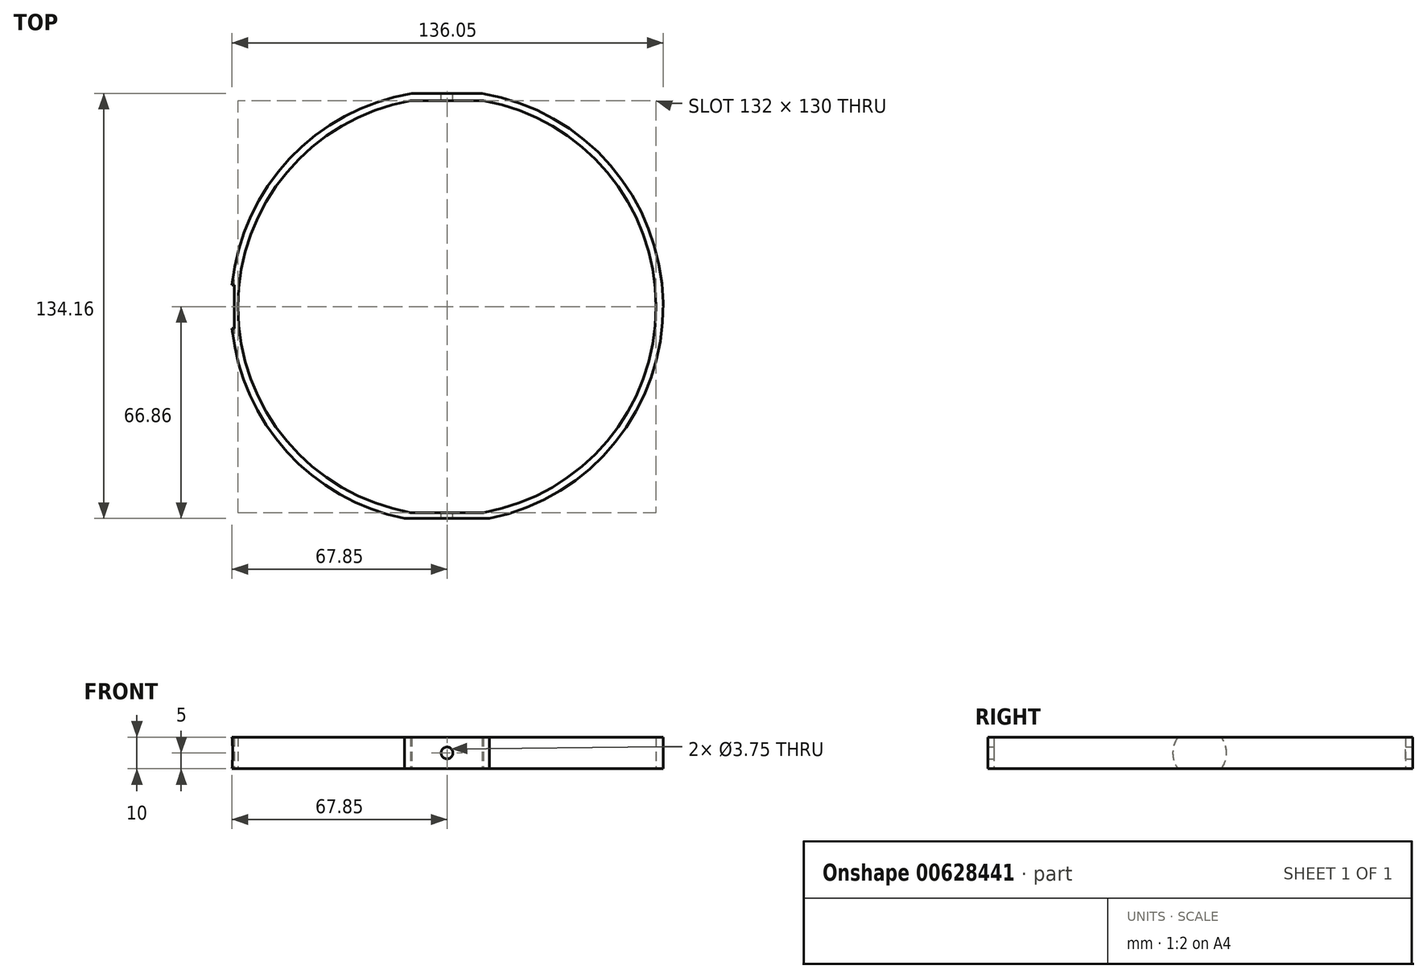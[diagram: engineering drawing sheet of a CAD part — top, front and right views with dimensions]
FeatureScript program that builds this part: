
annotation { "Feature Type Name" : "Feature", "Feature Type Description" : "" }
export const myFeature = defineFeature(function(context is Context, id is Id, definition is map)
    precondition{}
    {
        {
            var Q0;
            Q0=qCreatedBy(makeId("Top.planeOp"),FACE);
            var sketch = newSketch(context, id + "F0", { "sketchPlane" : qUnion([Q0])});
            skLineSegment(sketch, "E0", {"start": v(0, 0) * mm, "end": v(0, 65) * mm});
            skLineSegment(sketch, "E1", {"start": v(0, 0) * mm, "end": v(-66, 0) * mm});
            skArc(sketch, "E2", {"start": v(-11.45, 65) * mm, "mid": v(-66, 0) * mm, "end": v(-11.45, -65) * mm});
            skLineSegment(sketch, "E3.MirrorCS", {"start": v(0, 0) * mm, "end": v(66, 0) * mm});
            skLineSegment(sketch, "E4.MirrorCS", {"start": v(0, 0) * mm, "end": v(0, -65) * mm});
            skLineSegment(sketch, "E5", {"start": v(0, 65) * mm, "end": v(-11.45, 65) * mm});
            skLineSegment(sketch, "E6", {"start": v(-11.45, 65) * mm, "end": v(11.45, 65) * mm});
            skLineSegment(sketch, "E7", {"start": v(0, -65) * mm, "end": v(-11.45, -65) * mm});
            skLineSegment(sketch, "E8", {"start": v(-11.45, -65) * mm, "end": v(11.45, -65) * mm});
            skArc(sketch, "E9.trimOffspring", {"start": v(11.45, -65) * mm, "mid": v(66, 0) * mm, "end": v(11.45, 65) * mm});
            skArc(sketch, "E10", {"start": v(13.44, -66.86) * mm, "mid": v(68.2, 1.2) * mm, "end": v(11.08, 67.3) * mm});
            skLineSegment(sketch, "E11", {"start": v(0, 67.3) * mm, "end": v(-11.08, 67.3) * mm});
            skLineSegment(sketch, "E12", {"start": v(0, 67.3) * mm, "end": v(11.08, 67.3) * mm});
            skLineSegment(sketch, "E13", {"start": v(11.08, 67.3) * mm, "end": v(0, 67.3) * mm});
            skLineSegment(sketch, "E14", {"start": v(0, -66.86) * mm, "end": v(-13.44, -66.86) * mm});
            skLineSegment(sketch, "E15", {"start": v(-13.44, -66.86) * mm, "end": v(13.44, -66.86) * mm});
            skLineSegment(sketch, "E16", {"start": v(13.44, -66.86) * mm, "end": v(0, -66.86) * mm});
            skArc(sketch, "E17.trimOffspring", {"start": v(-11.08, 67.3) * mm, "mid": v(-68.2, 1.2) * mm, "end": v(-13.44, -66.86) * mm});
            skSolve(sketch);
        }
        {
            var Q0;
            Q0 = qSketchRegion(id + "F0", true);
            extrude(context, id + "F1", {"entities" : qUnion([Q0]), "depth" : 10 * mm, "offsetDistance" : 25 * mm});
        }
        {
            var Q0;
            Q0=makeQuery(id+"F1.opExtrude","SWEPT_FACE",FACE,{"disambiguationData":[OSD([sQuery(id+"F0.wireOp",EDGE,"E11"),sQuery(id+"F0.wireOp",EDGE,"E13")])]});
            var sketch = newSketch(context, id + "F2", { "sketchPlane" : qUnion([Q0])});
            skLineSegment(sketch, "E18", {"start": v(0, 0) * mm, "end": v(0, 10) * mm});
            skCircle(sketch, "E19", {"center": v(0, 5) * mm, "radius": 1.88 * mm});
            skSolve(sketch);
        }
        {
            var Q0;
            Q0 = qSketchRegion(id + "F2", true);
            extrude(context, id + "F3", {"entities" : qUnion([Q0]), "operationType" : NewBodyOperationType.REMOVE, "oppositeDirection" : true, "depth" : 170 * mm, "offsetDistance" : 25 * mm});
        }
        {
            var Q0;
            Q0=makeQuery(id+"F1.opExtrude","CAP_FACE",FACE,{"disambiguationData":[OSD([sQuery(id+"F0.wireOp",EDGE,"E2"),sQuery(id+"F0.wireOp",EDGE,"E6"),sQuery(id+"F0.wireOp",EDGE,"E8"),sQuery(id+"F0.wireOp",EDGE,"E9.trimOffspring"),sQuery(id+"F0.wireOp",EDGE,"E10"),sQuery(id+"F0.wireOp",EDGE,"E11"),sQuery(id+"F0.wireOp",EDGE,"E13"),sQuery(id+"F0.wireOp",EDGE,"E15"),sQuery(id+"F0.wireOp",EDGE,"E16"),sQuery(id+"F0.wireOp",EDGE,"E17.trimOffspring")])],"isStart":false});
            var sketch = newSketch(context, id + "F4", { "sketchPlane" : qUnion([Q0])});
            skLineSegment(sketch, "E20.bottom", {"start": v(-70.66, 2.4) * mm, "end": v(-66.61, 2.4) * mm});
            skLineSegment(sketch, "E20.top", {"start": v(-70.66, -2.4) * mm, "end": v(-66.61, -2.4) * mm});
            skLineSegment(sketch, "E20.left", {"start": v(-70.66, 2.4) * mm, "end": v(-70.66, -2.4) * mm});
            skPoint(sketch, "E20.middle", {"position": v(-66, 0) * mm});
            skLineSegment(sketch, "E21", {"start": v(-66.61, -2.4) * mm, "end": v(-66.61, 2.4) * mm});
            skPoint(sketch, "E20.right.end.orphan", {"position": v(-61.34, -2.4) * mm});
            skPoint(sketch, "E22.orphan", {"position": v(-61.34, 2.4) * mm});
            skSolve(sketch);
        }
        {
            var Q0;
            Q0 = qSketchRegion(id + "F4", true);
            extrude(context, id + "F5", {"entities" : qUnion([Q0]), "operationType" : NewBodyOperationType.REMOVE, "oppositeDirection" : true, "depth" : 25 * mm, "offsetDistance" : 25 * mm});
        }
        {
            var Q0;
            Q0=makeQuery(id+"F5.boolean.opBoolean","COPY",FACE,{"derivedFrom":makeQuery(id+"F5.opExtrude","SWEPT_FACE",FACE,{"disambiguationData":[OSD([sQuery(id+"F4.wireOp",EDGE,"E21")])]})});
            var sketch = newSketch(context, id + "F6", { "sketchPlane" : qUnion([Q0])});
            skLineSegment(sketch, "E23.bottom", {"start": v(-2.4, 10) * mm, "end": v(2.4, 10) * mm});
            skLineSegment(sketch, "E23.top", {"start": v(-2.4, 0) * mm, "end": v(2.4, 0) * mm});
            skLineSegment(sketch, "E23.left", {"start": v(-2.4, 10) * mm, "end": v(-2.4, 0) * mm});
            skLineSegment(sketch, "E23.right", {"start": v(2.4, 10) * mm, "end": v(2.4, 0) * mm});
            skSolve(sketch);
        }
        {
            var Q0;
            Q0 = qSketchRegion(id + "F6", true);
            extrude(context, id + "F7", {"entities" : qUnion([Q0]), "operationType" : NewBodyOperationType.ADD, "depth" : 1.55 * mm, "offsetDistance" : 25 * mm});
        }
        {
            var Q0;
            Q0=makeQuery(id+"F7.opExtrude","CAP_FACE",FACE,{"disambiguationData":[OSD([sQuery(id+"F6.wireOp",EDGE,"E23.bottom"),sQuery(id+"F6.wireOp",EDGE,"E23.top"),sQuery(id+"F6.wireOp",EDGE,"E23.left"),sQuery(id+"F6.wireOp",EDGE,"E23.right")])],"isStart":false});
            var sketch = newSketch(context, id + "F8", { "sketchPlane" : qUnion([Q0])});
            skLineSegment(sketch, "E24", {"start": v(0, 0) * mm, "end": v(0, 10) * mm});
            skCircle(sketch, "E25", {"center": v(0, 5) * mm, "radius": 8.5 * mm});
            skSolve(sketch);
        }
        {
            var Q0;
            Q0 = qSketchRegion(id + "F8", true);
            extrude(context, id + "F9", {"entities" : qUnion([Q0]), "operationType" : NewBodyOperationType.REMOVE, "oppositeDirection" : true, "depth" : 1 * mm, "offsetDistance" : 25 * mm});
        }
    });
